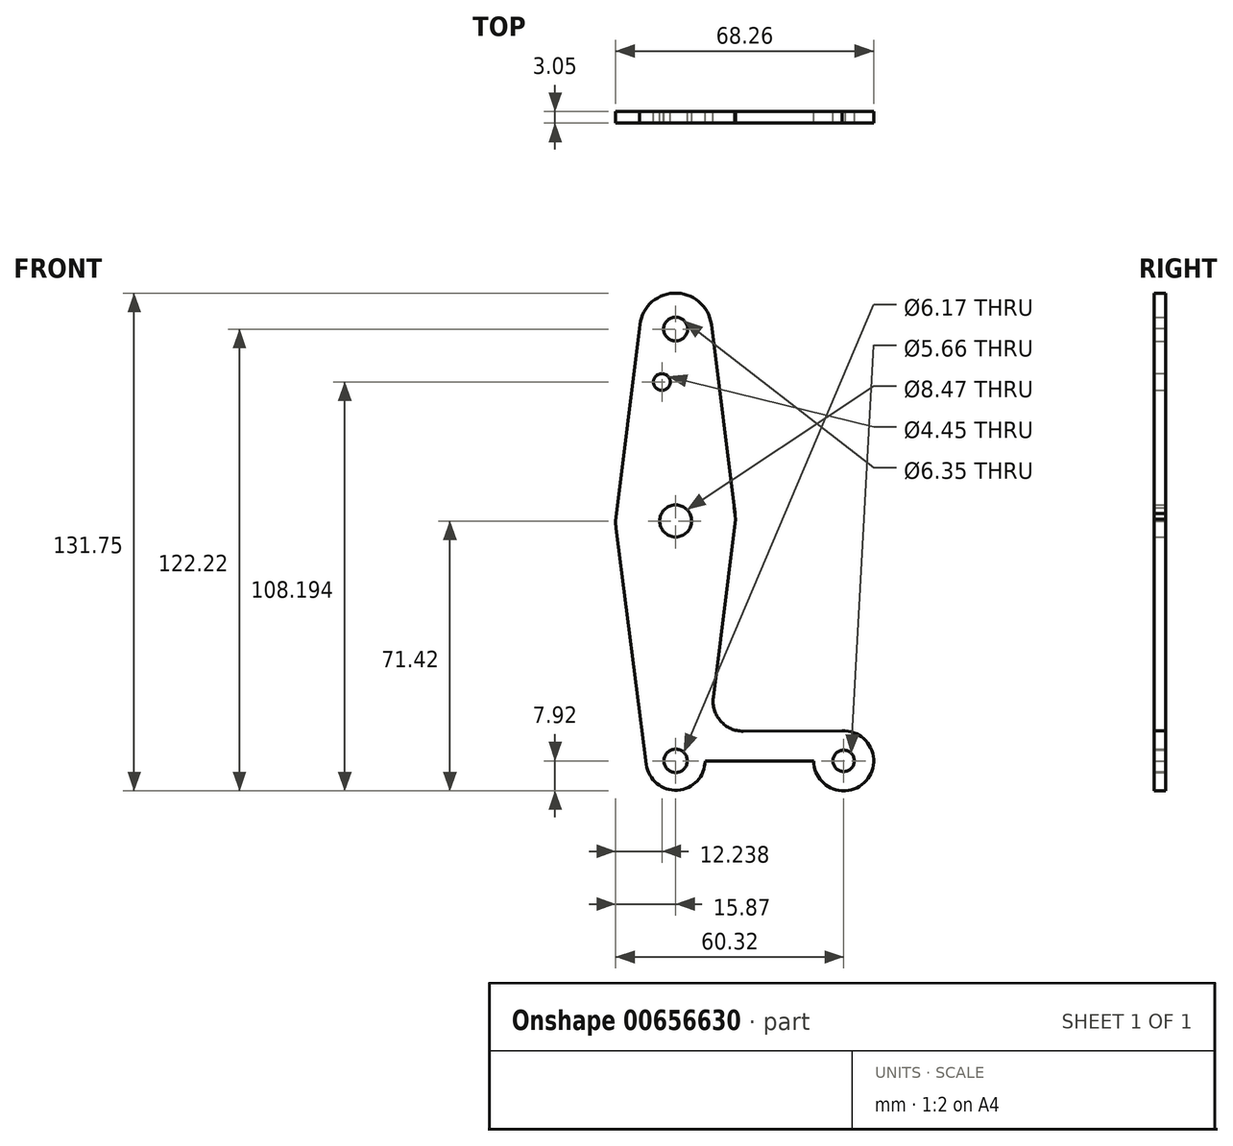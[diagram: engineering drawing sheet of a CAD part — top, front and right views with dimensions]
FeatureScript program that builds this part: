
annotation { "Feature Type Name" : "Feature", "Feature Type Description" : "" }
export const myFeature = defineFeature(function(context is Context, id is Id, definition is map)
    precondition{}
    {
        {
            var Q0;
            Q0=qCreatedBy(makeId("Front.planeOp"),FACE);
            var sketch = newSketch(context, id + "F0", { "sketchPlane" : qUnion([Q0])});
            skLineSegment(sketch, "E0", {"start": v(0, 0) * mm, "end": v(0, 63.5) * mm});
            skLineSegment(sketch, "E1", {"start": v(0, 63.5) * mm, "end": v(0, 114.3) * mm});
            skCircle(sketch, "E2", {"center": v(0, 114.3) * mm, "radius": 9.53 * mm});
            skCircle(sketch, "E3", {"center": v(0, 63.5) * mm, "radius": 15.88 * mm});
            skCircle(sketch, "E4", {"center": v(0, 0) * mm, "radius": 7.8 * mm});
            skLineSegment(sketch, "E5", {"start": v(0, 0) * mm, "end": v(44.45, 0) * mm});
            skCircle(sketch, "E6", {"center": v(44.45, 0) * mm, "radius": 7.94 * mm});
            skLineSegment(sketch, "E7", {"start": v(-9.52, 114.53) * mm, "end": v(-15.87, 63.44) * mm});
            skLineSegment(sketch, "E8", {"start": v(15.48, 67.01) * mm, "end": v(15.87, 64) * mm});
            skLineSegment(sketch, "E9", {"start": v(44.04, 7.93) * mm, "end": v(17.87, 7.85) * mm});
            skLineSegment(sketch, "E10", {"start": v(44.93, -7.92) * mm, "end": v(0, -7.8) * mm});
            skLineSegment(sketch, "E11", {"start": v(15.87, 64) * mm, "end": v(9.96, 16.79) * mm});
            skCircle(sketch, "E12", {"center": v(0, 114.3) * mm, "radius": 3.17 * mm});
            skCircle(sketch, "E13", {"center": v(0, 63.5) * mm, "radius": 4.24 * mm});
            skCircle(sketch, "E14", {"center": v(0, 0) * mm, "radius": 3.09 * mm});
            skCircle(sketch, "E15", {"center": v(44.45, 0) * mm, "radius": 2.83 * mm});
            skCircle(sketch, "E16", {"center": v(-3.63, 100.27) * mm, "radius": 2.22 * mm});
            skPoint(sketch, "E17.newPointA", {"position": v(7.86, 0) * mm});
            skArc(sketch, "E17.filletArc", {"start": v(9.96, 16.79) * mm, "mid": v(11.9, 10.53) * mm, "end": v(17.87, 7.85) * mm});
            skLineSegment(sketch, "E18", {"start": v(-7.73, -1) * mm, "end": v(-15.75, 61.48) * mm});
            skLineSegment(sketch, "E19", {"start": v(9.45, 115.5) * mm, "end": v(15.75, 65.48) * mm});
            skSolve(sketch);
        }
        {
            var Q0;
            {var subQ4=sQuery(id+"F0.wireOp",EDGE,"E19");Q0=makeQuery(id+"F0.imprint","IMPRINT",FACE,{"disambiguationData":[TD([[makeQuery(id+"F0.imprint","IMPRINT",EDGE,{"derivedFrom":subQ4}),-1.0]])]});}
            var Q1;
            Q1=makeQuery(id+"F0.imprint","IMPRINT",FACE,{"disambiguationData":[TD([[makeQuery(id+"F0.imprint","IMPRINT",EDGE,{"derivedFrom":sQuery(id+"F0.wireOp",EDGE,"E16")}),-1.0]])]});
            var Q2;
            Q2=makeQuery(id+"F0.imprint","IMPRINT",FACE,{"disambiguationData":[TD([[makeQuery(id+"F0.imprint","IMPRINT",EDGE,{"derivedFrom":sQuery(id+"F0.wireOp",EDGE,"E12")}),-1.0]])]});
            var Q3;
            {var subQ9=sQuery(id+"F0.wireOp",EDGE,"E8");Q3=makeQuery(id+"F0.imprint","IMPRINT",FACE,{"disambiguationData":[TD([[makeQuery(id+"F0.imprint","IMPRINT",EDGE,{"derivedFrom":subQ9}),-1.0]])]});}
            var Q4;
            {var subQ1=sQuery(id+"F0.wireOp",EDGE,"E3");var subQ5=sQuery(id+"F0.wireOp",EDGE,"E0");var subQ6=makeQuery(id+"F0.imprint","INTERSECT",VERTEX,{"derivedFrom":[subQ5,subQ1]});Q4=makeQuery(id+"F0.imprint","IMPRINT",FACE,{"disambiguationData":[TD([[makeQuery(id+"F0.imprint","IMPRINT",EDGE,{"disambiguationData":[TD([[subQ6,-1.0]])],"derivedFrom":subQ5}),1.0]])]});}
            var Q5;
            {var subQ5=sQuery(id+"F0.wireOp",EDGE,"E18");Q5=makeQuery(id+"F0.imprint","IMPRINT",FACE,{"disambiguationData":[TD([[makeQuery(id+"F0.imprint","IMPRINT",EDGE,{"derivedFrom":subQ5}),-1.0]])]});}
            var Q6;
            {var subQ7=sQuery(id+"F0.wireOp",EDGE,"E9");Q6=makeQuery(id+"F0.imprint","IMPRINT",FACE,{"disambiguationData":[TD([[makeQuery(id+"F0.imprint","IMPRINT",EDGE,{"derivedFrom":subQ7}),1.0]])]});}
            var Q7;
            {var subQ0=sQuery(id+"F0.wireOp",EDGE,"E10");var subQ1=sQuery(id+"F0.wireOp",EDGE,"E4");var subQ2=makeQuery(id+"F0.imprint","INTERSECT",VERTEX,{"derivedFrom":[subQ1,subQ0]});Q7=makeQuery(id+"F0.imprint","IMPRINT",FACE,{"disambiguationData":[TD([[makeQuery(id+"F0.imprint","IMPRINT",EDGE,{"disambiguationData":[TD([[subQ2,-1.0]])],"derivedFrom":subQ1}),-1.0]])]});}
            var Q8;
            {var subQ5=sQuery(id+"F0.wireOp",EDGE,"E0");var subQ7=sQuery(id+"F0.wireOp",EDGE,"E14");var subQ8=makeQuery(id+"F0.imprint","INTERSECT",VERTEX,{"derivedFrom":[subQ5,subQ7]});Q8=makeQuery(id+"F0.imprint","IMPRINT",FACE,{"disambiguationData":[TD([[makeQuery(id+"F0.imprint","IMPRINT",EDGE,{"disambiguationData":[TD([[subQ8,-1.0]])],"derivedFrom":subQ5}),1.0]])]});}
            var Q9;
            {var subQ0=sQuery(id+"F0.wireOp",EDGE,"E14");var subQ1=sQuery(id+"F0.wireOp",EDGE,"E0");var subQ2=makeQuery(id+"F0.imprint","INTERSECT",VERTEX,{"derivedFrom":[subQ1,subQ0]});Q9=makeQuery(id+"F0.imprint","IMPRINT",FACE,{"disambiguationData":[TD([[makeQuery(id+"F0.imprint","IMPRINT",EDGE,{"disambiguationData":[TD([[subQ2,-1.0]])],"derivedFrom":subQ1}),-1.0]])]});}
            var Q10;
            Q10=makeQuery(id+"F0.imprint","IMPRINT",FACE,{"disambiguationData":[TD([[makeQuery(id+"F0.imprint","IMPRINT",EDGE,{"derivedFrom":sQuery(id+"F0.wireOp",EDGE,"E15")}),-1.0]])]});
            extrude(context, id + "F1", {"entities" : qUnion([Q0, Q1, Q2, Q3, Q4, Q5, Q6, Q7, Q8, Q9, Q10]), "depth" : 3.05 * mm, "offsetDistance" : 25.4 * mm});
        }
    });
